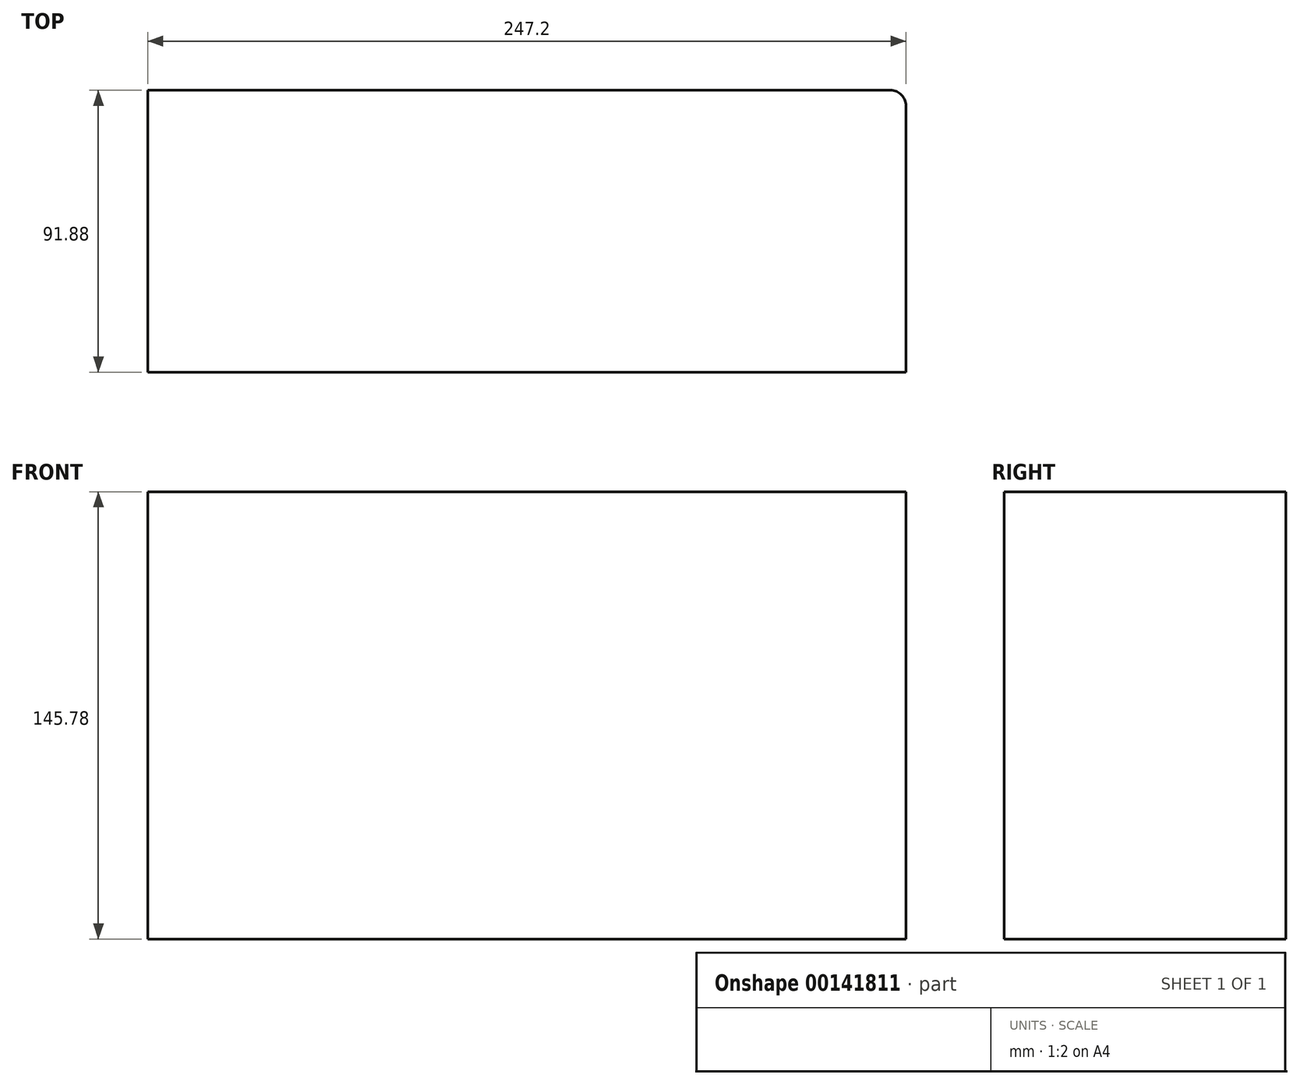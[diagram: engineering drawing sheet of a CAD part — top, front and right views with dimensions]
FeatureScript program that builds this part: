
annotation { "Feature Type Name" : "Feature", "Feature Type Description" : "" }
export const myFeature = defineFeature(function(context is Context, id is Id, definition is map)
    precondition{}
    {
        {
            var Q0;
            Q0=qCreatedBy(makeId("Front.planeOp"),FACE);
            var sketch = newSketch(context, id + "F0", { "sketchPlane" : qUnion([Q0])});
            skLineSegment(sketch, "E0.bottom", {"start": v(-123.6, -72.9) * mm, "end": v(123.6, -72.9) * mm});
            skLineSegment(sketch, "E0.top", {"start": v(-123.6, 72.9) * mm, "end": v(123.6, 72.9) * mm});
            skLineSegment(sketch, "E0.left", {"start": v(-123.6, -72.9) * mm, "end": v(-123.6, 72.9) * mm});
            skLineSegment(sketch, "E0.right", {"start": v(123.6, -72.9) * mm, "end": v(123.6, 72.9) * mm});
            skPoint(sketch, "E0.middle", {"position": v(0, 0) * mm});
            skSolve(sketch);
        }
        {
            var Q0;
            Q0 = qSketchRegion(id + "F0", true);
            extrude(context, id + "F1", {"entities" : qUnion([Q0]), "oppositeDirection" : true, "depth" : 91.88 * mm});
        }
        {
            var Q0;
            Q0=makeQuery(id+"F1.opExtrude","CAP_EDGE",EDGE,{"disambiguationData":[OSD([sQuery(id+"F0.wireOp",EDGE,"E0.right")])],"isStart":false});
            fillet(context, id + "F2", {"entities" : qUnion([Q0]), "radius" : 5.08 * mm, "tangentPropagation" : true, "allowEdgeOverflow" : false});
        }
    });
